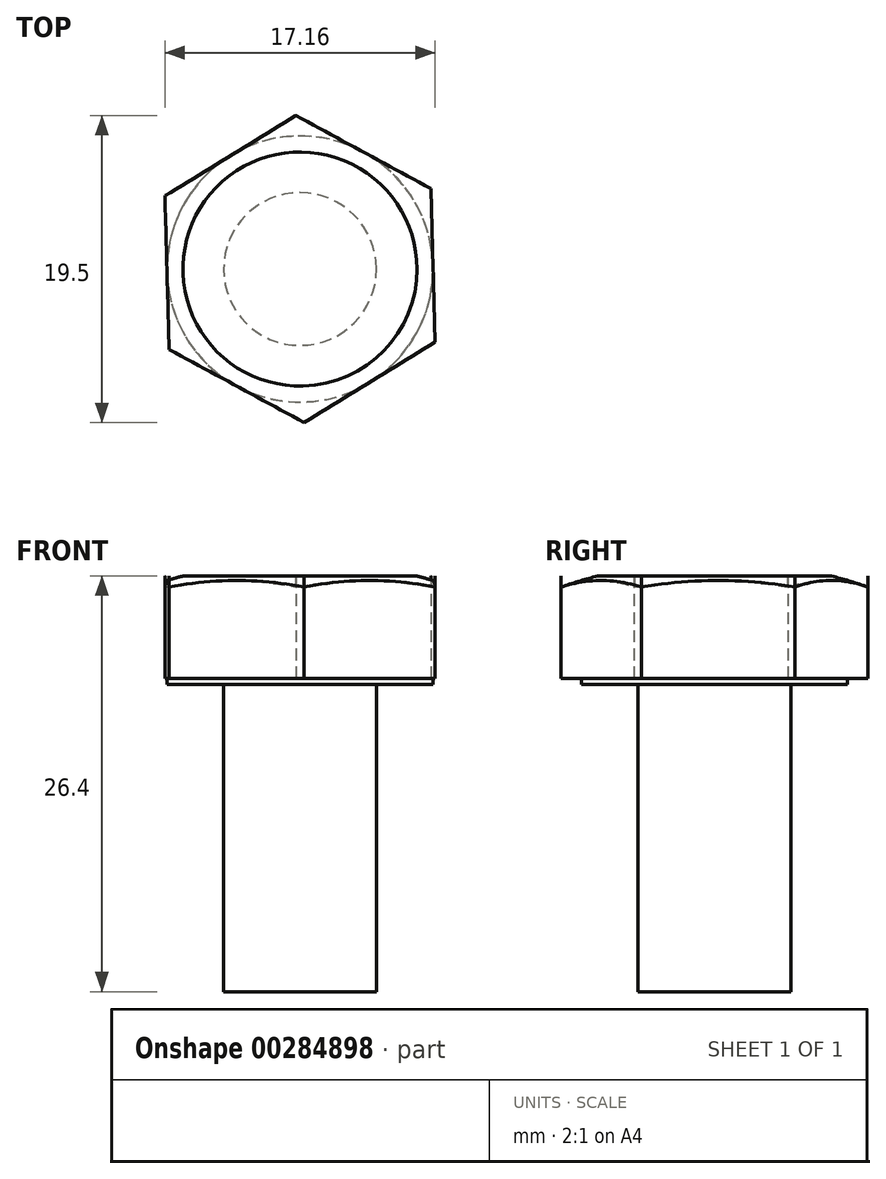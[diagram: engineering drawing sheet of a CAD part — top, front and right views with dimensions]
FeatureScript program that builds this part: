
annotation { "Feature Type Name" : "Feature", "Feature Type Description" : "" }
export const myFeature = defineFeature(function(context is Context, id is Id, definition is map)
    precondition{}
    {
        {
            var Q0;
            Q0=qCreatedBy(makeId("Front.planeOp"),FACE);
            var sketch = newSketch(context, id + "F0", { "sketchPlane" : qUnion([Q0])});
            skLineSegment(sketch, "E0", {"start": v(-4.85, 26.53) * mm, "end": v(-4.85, 7.03) * mm});
            skLineSegment(sketch, "E1", {"start": v(-4.85, 7.03) * mm, "end": v(0, 7.03) * mm});
            skLineSegment(sketch, "E2", {"start": v(-4.85, 26.53) * mm, "end": v(-8.45, 26.53) * mm});
            skLineSegment(sketch, "E3", {"start": v(-8.45, 26.53) * mm, "end": v(-8.45, 26.93) * mm});
            skLineSegment(sketch, "E4", {"start": v(-8.45, 26.93) * mm, "end": v(0, 26.93) * mm});
            skLineSegment(sketch, "E5", {"start": v(0, 26.93) * mm, "end": v(0, 7.03) * mm});
            skSolve(sketch);
        }
        {
            var Q0;
            Q0=makeQuery(id+"F0.imprint","IMPRINT",FACE,{"disambiguationData":[TD([[makeQuery(id+"F0.imprint","IMPRINT",EDGE,{"derivedFrom":sQuery(id+"F0.wireOp",EDGE,"E0")}),1.0]])]});
            var Q1;
            Q1=sQuery(id+"F0.wireOp",EDGE,"E5");
            revolve(context, id + "F1", {"surfaceOperationType" : NewSurfaceOperationType.NEW, "entities" : qUnion([Q0]), "axis" : qUnion([Q1]), "revolveType" : RevolveType.FULL});
        }
        {
            var Q0;
            Q0=makeQuery(id+"F1.opRevolve","SWEPT_FACE",FACE,{"disambiguationData":[OSD([sQuery(id+"F0.wireOp",EDGE,"E4")])]});
            var sketch = newSketch(context, id + "F2", { "sketchPlane" : qUnion([Q0])});
            skCircle(sketch, "E6.cCircle", {"center": v(0, 0) * mm, "radius": 8.45 * mm, "construction": true});
            skLineSegment(sketch, "E6.0", {"start": v(-8.58, 4.65) * mm, "end": v(-0.27, 9.75) * mm});
            skLineSegment(sketch, "E6.1", {"start": v(-0.27, 9.75) * mm, "end": v(8.31, 5.1) * mm});
            skLineSegment(sketch, "E6.2", {"start": v(8.31, 5.1) * mm, "end": v(8.58, -4.65) * mm});
            skLineSegment(sketch, "E6.3", {"start": v(8.58, -4.65) * mm, "end": v(0.27, -9.75) * mm});
            skLineSegment(sketch, "E6.4", {"start": v(0.27, -9.75) * mm, "end": v(-8.31, -5.1) * mm});
            skLineSegment(sketch, "E6.5", {"start": v(-8.31, -5.1) * mm, "end": v(-8.58, 4.65) * mm});
            skPoint(sketch, "E6.0.midPoint", {"position": v(-4.42, 7.2) * mm});
            skSolve(sketch);
        }
        {
            var Q0;
            {var subQ0=sQuery(id+"F2.wireOp",EDGE,"E6.5");var subQ1=sQuery(id+"F2.wireOp",EDGE,"E6.0");var subQ2=makeQuery(id+"F2.imprint","INTERSECT",VERTEX,{"derivedFrom":[subQ1,subQ0]});Q0=makeQuery(id+"F2.imprint","IMPRINT",FACE,{"disambiguationData":[TD([[makeQuery(id+"F2.imprint","IMPRINT",EDGE,{"disambiguationData":[TD([[subQ2,-1.0]])],"derivedFrom":subQ1}),-1.0]])]});}
            var Q1;
            {var subQ0=sQuery(id+"F2.wireOp",EDGE,"E6.5");var subQ1=sQuery(id+"F2.wireOp",EDGE,"E6.4");var subQ2=makeQuery(id+"F2.imprint","INTERSECT",VERTEX,{"derivedFrom":[subQ1,subQ0]});Q1=makeQuery(id+"F2.imprint","IMPRINT",FACE,{"disambiguationData":[TD([[makeQuery(id+"F2.imprint","IMPRINT",EDGE,{"disambiguationData":[TD([[subQ2,1.0]])],"derivedFrom":subQ1}),-1.0]])]});}
            var Q2;
            {var subQ0=sQuery(id+"F2.wireOp",EDGE,"E6.4");var subQ1=sQuery(id+"F2.wireOp",EDGE,"E6.3");var subQ2=makeQuery(id+"F2.imprint","INTERSECT",VERTEX,{"derivedFrom":[subQ1,subQ0]});Q2=makeQuery(id+"F2.imprint","IMPRINT",FACE,{"disambiguationData":[TD([[makeQuery(id+"F2.imprint","IMPRINT",EDGE,{"disambiguationData":[TD([[subQ2,1.0]])],"derivedFrom":subQ1}),-1.0]])]});}
            var Q3;
            {var subQ0=sQuery(id+"F2.wireOp",EDGE,"E6.3");var subQ1=sQuery(id+"F2.wireOp",EDGE,"E6.2");var subQ2=makeQuery(id+"F2.imprint","INTERSECT",VERTEX,{"derivedFrom":[subQ1,subQ0]});Q3=makeQuery(id+"F2.imprint","IMPRINT",FACE,{"disambiguationData":[TD([[makeQuery(id+"F2.imprint","IMPRINT",EDGE,{"disambiguationData":[TD([[subQ2,1.0]])],"derivedFrom":subQ1}),-1.0]])]});}
            var Q4;
            {var subQ0=sQuery(id+"F2.wireOp",EDGE,"E6.2");var subQ1=sQuery(id+"F2.wireOp",EDGE,"E6.1");var subQ2=makeQuery(id+"F2.imprint","INTERSECT",VERTEX,{"derivedFrom":[subQ1,subQ0]});Q4=makeQuery(id+"F2.imprint","IMPRINT",FACE,{"disambiguationData":[TD([[makeQuery(id+"F2.imprint","IMPRINT",EDGE,{"disambiguationData":[TD([[subQ2,1.0]])],"derivedFrom":subQ1}),-1.0]])]});}
            var Q5;
            {var subQ0=sQuery(id+"F2.wireOp",EDGE,"E6.1");var subQ1=sQuery(id+"F2.wireOp",EDGE,"E6.0");var subQ2=makeQuery(id+"F2.imprint","INTERSECT",VERTEX,{"derivedFrom":[subQ1,subQ0]});Q5=makeQuery(id+"F2.imprint","IMPRINT",FACE,{"disambiguationData":[TD([[makeQuery(id+"F2.imprint","IMPRINT",EDGE,{"disambiguationData":[TD([[subQ2,1.0]])],"derivedFrom":subQ1}),-1.0]])]});}
            var Q6;
            {var subQ0=makeQuery(id+"F1.opRevolve","SWEPT_EDGE",EDGE,{"disambiguationData":[OSD([sQuery(id+"F0.wireOp",EDGE,"E3"),sQuery(id+"F0.wireOp",EDGE,"E4")])]});var subQ4=makeQuery(id+"F2.imprint","INTERSECT",VERTEX,{"derivedFrom":[subQ0,sQuery(id+"F2.wireOp",EDGE,"E6.0")]});Q6=makeQuery(id+"F2.imprint","IMPRINT",FACE,{"disambiguationData":[TD([[makeQuery(id+"F2.imprint","IMPRINT",EDGE,{"disambiguationData":[TD([[subQ4,1.0]])],"derivedFrom":subQ0}),1.0]])]});}
            extrude(context, id + "F3", {"entities" : qUnion([Q0, Q1, Q2, Q3, Q4, Q5, Q6]), "operationType" : NewBodyOperationType.ADD, "depth" : 6.5 * mm, "offsetDistance" : 25.4 * mm});
        }
        {
            var Q0;
            Q0=qCreatedBy(makeId("Right.planeOp"),FACE);
            var sketch = newSketch(context, id + "F4", { "sketchPlane" : qUnion([Q0])});
            skLineSegment(sketch, "E7.0", {"start": v(9.75, 33.43) * mm, "end": v(9.75, 26.93) * mm});
            skLineSegment(sketch, "E8.0", {"start": v(-9.75, 33.43) * mm, "end": v(-9.75, 26.93) * mm});
            skArc(sketch, "E9", {"start": v(-0.6, 34.37) * mm, "mid": v(-5.24, 33.9) * mm, "end": v(-9.75, 32.73) * mm});
            skLineSegment(sketch, "E10", {"start": v(-9.75, 32.73) * mm, "end": v(-9.75, 34.18) * mm});
            skLineSegment(sketch, "E11", {"start": v(-9.75, 34.18) * mm, "end": v(0, 34.38) * mm});
            skPoint(sketch, "E12.orphan", {"position": v(9.75, 32.73) * mm});
            skLineSegment(sketch, "E13", {"start": v(0, 34.38) * mm, "end": v(0, 33.38) * mm, "construction": true});
            skSolve(sketch);
        }
        {
            var Q0;
            {var subQ0=sQuery(id+"F4.wireOp",EDGE,"E9");Q0=makeQuery(id+"F4.imprint","IMPRINT",FACE,{"disambiguationData":[TD([[makeQuery(id+"F4.imprint","IMPRINT",EDGE,{"derivedFrom":subQ0}),-1.0]])]});}
            var Q1;
            Q1=sQuery(id+"F4.wireOp",EDGE,"E13");
            revolve(context, id + "F5", {"operationType" : NewBodyOperationType.REMOVE, "surfaceOperationType" : NewSurfaceOperationType.NEW, "entities" : qUnion([Q0]), "axis" : qUnion([Q1]), "revolveType" : RevolveType.FULL, "oppositeDirection" : true});
        }
    });
